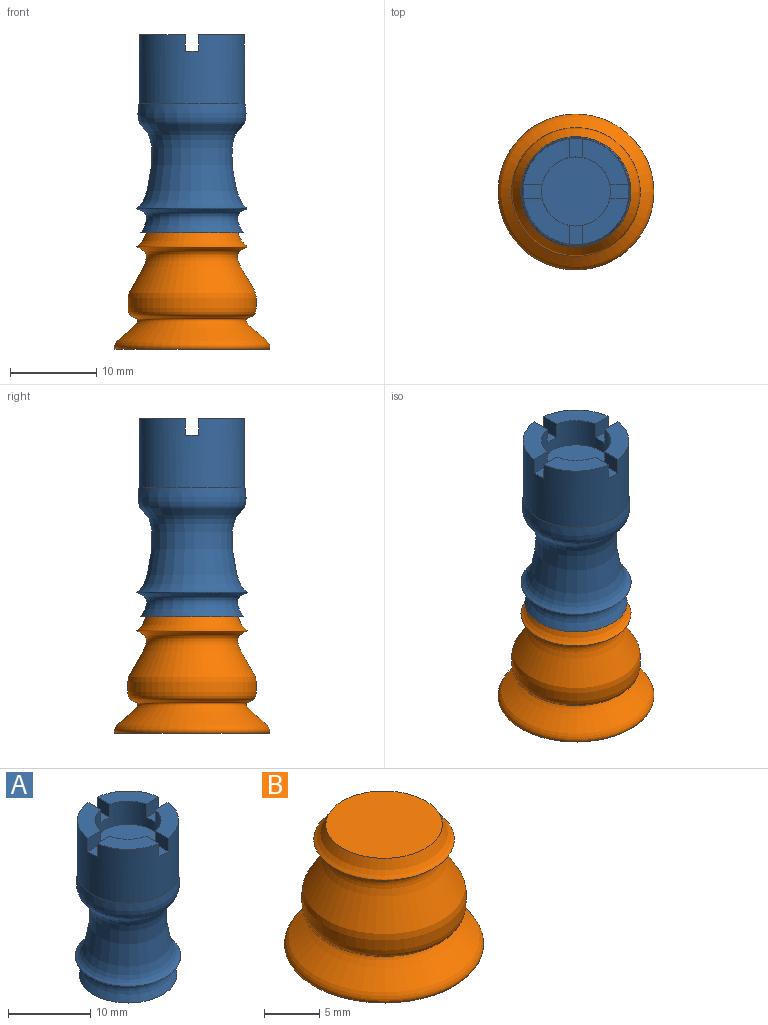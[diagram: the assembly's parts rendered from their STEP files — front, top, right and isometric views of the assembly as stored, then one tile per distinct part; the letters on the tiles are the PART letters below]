
ASSEMBLY  parts=2 mates=1
PART A: 21 faces, bbox 12.7x12.7x23 mm
  f0: cylinder r=4.01mm len=8.02mm, axis (0,0,1), area 74.6mm2, adj f1,f2,f3,f5,f8,f9,f10,f11
  f1: plane 5.41x5.41mm, normal (0,0,1), area 13.7mm2, adj f0,f4,f12,f19
  f2: plane 5.41x5.41mm, normal (0,0,1), area 13.7mm2, adj f0,f4,f10,f18
  f3: plane 5.41x5.41mm, normal (0,0,1), area 13.7mm2, adj f0,f4,f13,f15
  f4: cylinder r=6.15mm len=12.29mm, axis (0,0,1), area 296.8mm2, adj f1,f2,f3,f5,f6,f9,f10,f11
  f5: plane 5.41x5.41mm, normal (0,0,1), area 13.7mm2, adj f0,f4,f9,f17
  f6: revolved ~15x12.74mm, area 556.3mm2, adj f4,f7
  f7: plane 11.86x11.86mm, normal (0,0,-1), area 110.5mm2, adj f6
  f8: plane 8.02x8.02mm, normal (0,0,1), area 50.6mm2, adj f0
  f9: plane 2.16x1.96mm, normal (0,1,0), area 4.2mm2, adj f0,f4,f5,f11
  f10: plane 2.16x1.96mm, normal (0,-1,0), area 4.2mm2, adj f0,f2,f4,f11
  f11: plane 2.21x1.56mm, normal (0,0,1), area 3.3mm2, adj f0,f4,f9,f10
  f12: plane 2.16x1.96mm, normal (0,-1,0), area 4.2mm2, adj f0,f1,f4,f14
  f13: plane 2.16x1.96mm, normal (0,1,0), area 4.2mm2, adj f0,f3,f4,f14
  f14: plane 2.21x1.56mm, normal (0,0,1), area 3.3mm2, adj f0,f4,f12,f13
  f15: plane 2.16x1.96mm, normal (-1,0,0), area 4.2mm2, adj f0,f3,f4,f16
  f16: plane 2.21x1.56mm, normal (0,0,1), area 3.3mm2, adj f0,f4,f15,f17
  f17: plane 2.16x1.96mm, normal (1,0,0), area 4.2mm2, adj f0,f4,f5,f16
  f18: plane 2.16x1.96mm, normal (1,0,0), area 4.2mm2, adj f0,f2,f4,f20
  f19: plane 2.16x1.96mm, normal (-1,0,0), area 4.2mm2, adj f0,f1,f4,f20
  f20: plane 2.21x1.56mm, normal (0,0,1), area 3.3mm2, adj f0,f4,f18,f19
PART B: 3 faces, bbox 18x18x13.6 mm
  f0: plane 10.6x10.6mm, normal (0,0,1), area 88.3mm2, adj f1
  f1: revolved ~18.05x18.05mm, area 716mm2, adj f0,f2
  f2: cone r=8.96mm half-angle=89.7deg, axis (0,0,1), area 252.2mm2, adj f1
PLACE A t=(-11.49,16.76,0.28)mm
PLACE B t=(-11.49,16.76,-4.18)mm
MATE fastened B.f2 <-> A.f0  axis (0,0,1) through (-11.49,16.76,23.59)mm
